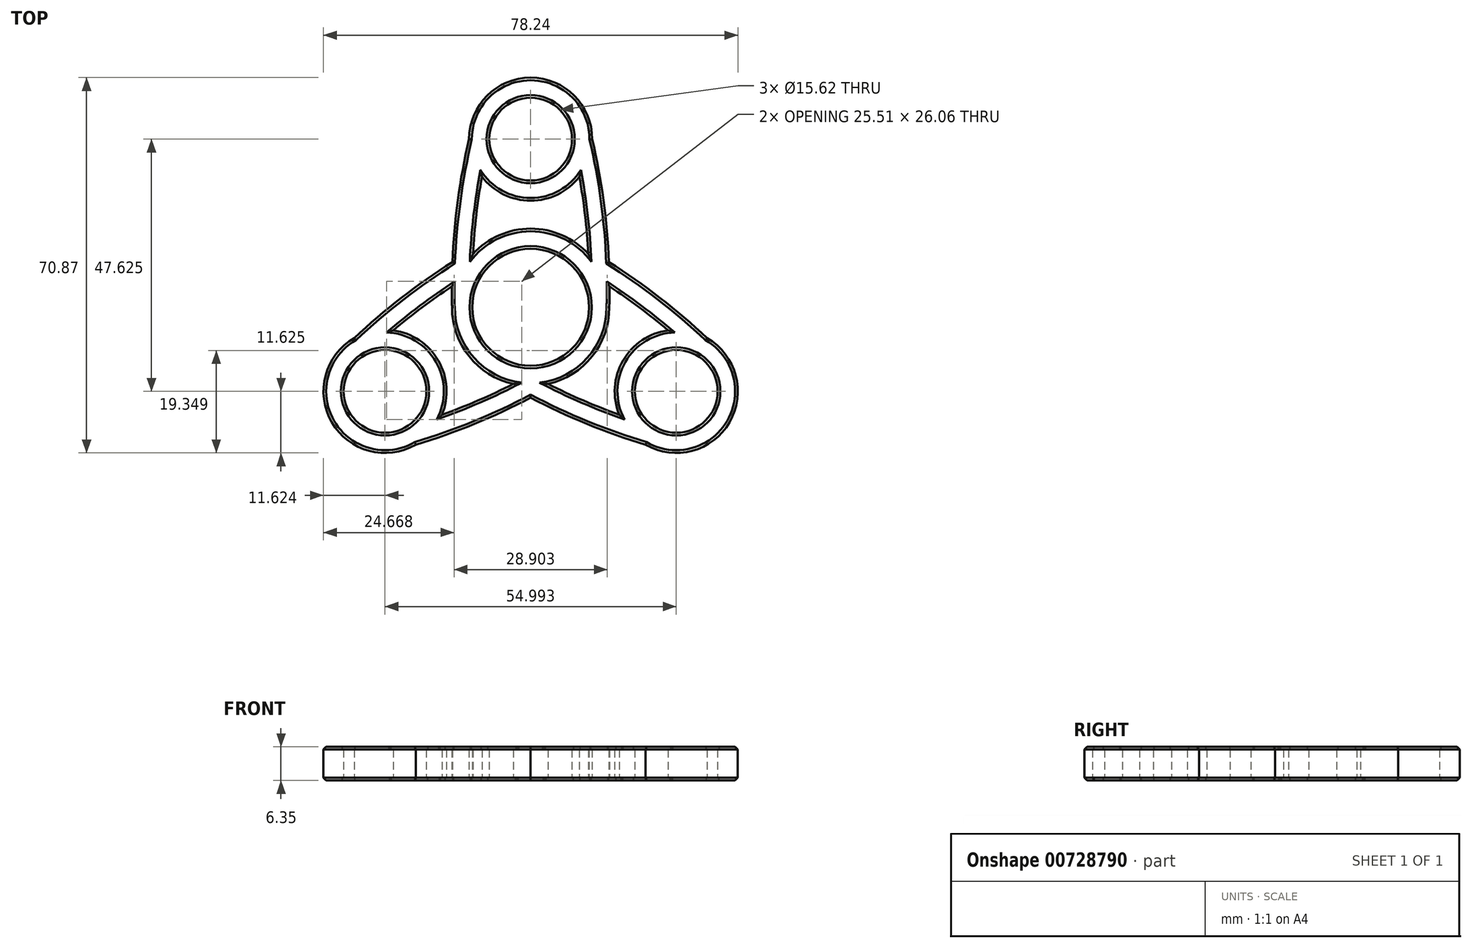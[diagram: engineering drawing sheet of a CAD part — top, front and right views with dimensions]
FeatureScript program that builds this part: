
annotation { "Feature Type Name" : "Feature", "Feature Type Description" : "" }
export const myFeature = defineFeature(function(context is Context, id is Id, definition is map)
    precondition{}
    {
        {
            var Q0;
            Q0=qCreatedBy(makeId("Top.planeOp"),FACE);
            var sketch = newSketch(context, id + "F0", { "sketchPlane" : qUnion([Q0])});
            skCircle(sketch, "E0", {"center": v(0, 0) * mm, "radius": 11.04 * mm});
            skPoint(sketch, "E1.orphan", {"position": v(-10.8, 40.16) * mm});
            skPoint(sketch, "E2.orphan", {"position": v(-5.54, 30.57) * mm});
            skPoint(sketch, "E3.orphan", {"position": v(10.8, 40.16) * mm});
            skPoint(sketch, "E4.start.orphan", {"position": v(0, 56) * mm});
            skCircle(sketch, "E5", {"center": v(0, 31.75) * mm, "radius": 7.81 * mm});
            skArc(sketch, "E6.0", {"start": v(-9.2, 24.65) * mm, "mid": v(0, 20.13) * mm, "end": v(9.2, 24.65) * mm});
            skArc(sketch, "E7.0", {"start": v(-14.85, 0) * mm, "mid": v(-11.6, -9.27) * mm, "end": v(-3.28, -14.48) * mm});
            skLineSegment(sketch, "E8", {"start": v(3.28, 31.75) * mm, "end": v(3.28, 31.75) * mm});
            skArc(sketch, "E9", {"start": v(-11.62, 31.75) * mm, "mid": v(-13.75, 20.22) * mm, "end": v(-14.79, 8.54) * mm});
            skArc(sketch, "E10.0", {"start": v(-9.2, 24.65) * mm, "mid": v(-10.27, 17.4) * mm, "end": v(-10.9, 10.08) * mm});
            skArc(sketch, "E11.MirrorCS", {"start": v(9.2, 24.65) * mm, "mid": v(10.27, 17.4) * mm, "end": v(10.9, 10.08) * mm});
            skArc(sketch, "E12.MirrorCS", {"start": v(11.62, 31.75) * mm, "mid": v(13.75, 20.22) * mm, "end": v(14.79, 8.54) * mm});
            skPoint(sketch, "E13.orphan", {"position": v(-7.91, 30.88) * mm});
            skPoint(sketch, "E14.orphan", {"position": v(-11.04, 0.1) * mm});
            skPoint(sketch, "E15.orphan", {"position": v(7.91, 30.88) * mm});
            skArc(sketch, "E16.trimOffspring", {"start": v(11.62, 31.75) * mm, "mid": v(0, 43.37) * mm, "end": v(-11.62, 31.75) * mm});
            skPoint(sketch, "E17.orphan", {"position": v(11.04, 0.1) * mm});
            skArc(sketch, "E18.trimOffspring", {"start": v(10.9, 10.08) * mm, "mid": v(0, 14.85) * mm, "end": v(-10.9, 10.08) * mm});
            skArc(sketch, "E19.1.0", {"start": v(-33.3, -5.81) * mm, "mid": v(-24.39, 1.8) * mm, "end": v(-14.79, 8.54) * mm});
            skArc(sketch, "E19.1.1", {"start": v(-25.95, -4.36) * mm, "mid": v(-20.54, -0.05) * mm, "end": v(-14.9, 3.93) * mm});
            skArc(sketch, "E19.1.2", {"start": v(-16.75, -20.3) * mm, "mid": v(-9.92, -17.6) * mm, "end": v(-3.28, -14.48) * mm});
            skArc(sketch, "E19.1.3", {"start": v(-16.75, -20.3) * mm, "mid": v(-17.43, -10.06) * mm, "end": v(-25.95, -4.36) * mm});
            skCircle(sketch, "E19.1.4", {"center": v(-27.5, -15.87) * mm, "radius": 7.81 * mm});
            skArc(sketch, "E19.1.5", {"start": v(-33.3, -5.81) * mm, "mid": v(-37.56, -21.69) * mm, "end": v(-21.69, -25.94) * mm});
            skArc(sketch, "E19.1.6", {"start": v(-21.69, -25.94) * mm, "mid": v(-10.63, -22.02) * mm, "end": v(0, -17.08) * mm});
            skArc(sketch, "E19.2.0", {"start": v(21.69, -25.94) * mm, "mid": v(10.63, -22.02) * mm, "end": v(0, -17.08) * mm});
            skArc(sketch, "E19.2.1", {"start": v(16.75, -20.3) * mm, "mid": v(9.92, -17.6) * mm, "end": v(3.28, -14.48) * mm});
            skArc(sketch, "E19.2.2", {"start": v(25.95, -4.36) * mm, "mid": v(20.54, -0.05) * mm, "end": v(14.9, 3.93) * mm});
            skArc(sketch, "E19.2.3", {"start": v(25.95, -4.36) * mm, "mid": v(17.43, -10.06) * mm, "end": v(16.75, -20.3) * mm});
            skCircle(sketch, "E19.2.4", {"center": v(27.5, -15.88) * mm, "radius": 7.81 * mm});
            skArc(sketch, "E19.2.5", {"start": v(21.69, -25.94) * mm, "mid": v(37.56, -21.69) * mm, "end": v(33.3, -5.81) * mm});
            skArc(sketch, "E19.2.6", {"start": v(33.3, -5.81) * mm, "mid": v(24.39, 1.8) * mm, "end": v(14.79, 8.54) * mm});
            skArc(sketch, "E20.trimOffspring", {"start": v(-14.9, 3.93) * mm, "mid": v(-14.89, 1.97) * mm, "end": v(-14.85, 0) * mm});
            skPoint(sketch, "E21.orphan", {"position": v(-14.18, 4.4) * mm});
            skPoint(sketch, "E22.orphan", {"position": v(7.42, -12.86) * mm});
            skArc(sketch, "E23.trimOffspring", {"start": v(3.28, -14.48) * mm, "mid": v(11.6, -9.27) * mm, "end": v(14.85, 0) * mm});
            skPoint(sketch, "E24.orphan", {"position": v(7.42, 12.86) * mm});
            skPoint(sketch, "E25.orphan", {"position": v(14.18, 4.4) * mm});
            skArc(sketch, "E26.trimOffspring", {"start": v(14.9, 3.93) * mm, "mid": v(14.89, 1.97) * mm, "end": v(14.85, 0) * mm});
            skSolve(sketch);
        }
        {
            var Q0;
            Q0=makeQuery(id+"F0.imprint","IMPRINT",FACE,{"disambiguationData":[TD([[makeQuery(id+"F0.imprint","IMPRINT",EDGE,{"derivedFrom":sQuery(id+"F0.wireOp",EDGE,"E0")}),-1.0]])]});
            extrude(context, id + "F1", {"entities" : qUnion([Q0]), "depth" : 6.35 * mm, "offsetDistance" : 25.4 * mm});
        }
        {
            var Q0;
            Q0=makeQuery(id+"F1.opExtrude","CAP_FACE",FACE,{"disambiguationData":[OSD([sQuery(id+"F0.wireOp",EDGE,"E0"),sQuery(id+"F0.wireOp",EDGE,"E5"),sQuery(id+"F0.wireOp",EDGE,"E6.0"),sQuery(id+"F0.wireOp",EDGE,"E7.0"),sQuery(id+"F0.wireOp",EDGE,"E9"),sQuery(id+"F0.wireOp",EDGE,"E10.0"),sQuery(id+"F0.wireOp",EDGE,"E11.MirrorCS"),sQuery(id+"F0.wireOp",EDGE,"E12.MirrorCS"),sQuery(id+"F0.wireOp",EDGE,"E16.trimOffspring"),sQuery(id+"F0.wireOp",EDGE,"E18.trimOffspring"),sQuery(id+"F0.wireOp",EDGE,"E19.1.0"),sQuery(id+"F0.wireOp",EDGE,"E19.1.1"),sQuery(id+"F0.wireOp",EDGE,"E19.1.2"),sQuery(id+"F0.wireOp",EDGE,"E19.1.3"),sQuery(id+"F0.wireOp",EDGE,"E19.1.4"),sQuery(id+"F0.wireOp",EDGE,"E19.1.5"),sQuery(id+"F0.wireOp",EDGE,"E19.1.6"),sQuery(id+"F0.wireOp",EDGE,"E19.2.0"),sQuery(id+"F0.wireOp",EDGE,"E19.2.1"),sQuery(id+"F0.wireOp",EDGE,"E19.2.2"),sQuery(id+"F0.wireOp",EDGE,"E19.2.3"),sQuery(id+"F0.wireOp",EDGE,"E19.2.4"),sQuery(id+"F0.wireOp",EDGE,"E19.2.5"),sQuery(id+"F0.wireOp",EDGE,"E19.2.6"),sQuery(id+"F0.wireOp",EDGE,"E20.trimOffspring"),sQuery(id+"F0.wireOp",EDGE,"E23.trimOffspring"),sQuery(id+"F0.wireOp",EDGE,"E26.trimOffspring")])],"isStart":false});
            var Q1;
            Q1=makeQuery(id+"F1.opExtrude","CAP_FACE",FACE,{"disambiguationData":[OSD([sQuery(id+"F0.wireOp",EDGE,"E0"),sQuery(id+"F0.wireOp",EDGE,"E5"),sQuery(id+"F0.wireOp",EDGE,"E6.0"),sQuery(id+"F0.wireOp",EDGE,"E7.0"),sQuery(id+"F0.wireOp",EDGE,"E9"),sQuery(id+"F0.wireOp",EDGE,"E10.0"),sQuery(id+"F0.wireOp",EDGE,"E11.MirrorCS"),sQuery(id+"F0.wireOp",EDGE,"E12.MirrorCS"),sQuery(id+"F0.wireOp",EDGE,"E16.trimOffspring"),sQuery(id+"F0.wireOp",EDGE,"E18.trimOffspring"),sQuery(id+"F0.wireOp",EDGE,"E19.1.0"),sQuery(id+"F0.wireOp",EDGE,"E19.1.1"),sQuery(id+"F0.wireOp",EDGE,"E19.1.2"),sQuery(id+"F0.wireOp",EDGE,"E19.1.3"),sQuery(id+"F0.wireOp",EDGE,"E19.1.4"),sQuery(id+"F0.wireOp",EDGE,"E19.1.5"),sQuery(id+"F0.wireOp",EDGE,"E19.1.6"),sQuery(id+"F0.wireOp",EDGE,"E19.2.0"),sQuery(id+"F0.wireOp",EDGE,"E19.2.1"),sQuery(id+"F0.wireOp",EDGE,"E19.2.2"),sQuery(id+"F0.wireOp",EDGE,"E19.2.3"),sQuery(id+"F0.wireOp",EDGE,"E19.2.4"),sQuery(id+"F0.wireOp",EDGE,"E19.2.5"),sQuery(id+"F0.wireOp",EDGE,"E19.2.6"),sQuery(id+"F0.wireOp",EDGE,"E20.trimOffspring"),sQuery(id+"F0.wireOp",EDGE,"E23.trimOffspring"),sQuery(id+"F0.wireOp",EDGE,"E26.trimOffspring")])],"isStart":true});
            chamfer(context, id + "F2", {"entities" : qUnion([Q0, Q1]), "width" : 0.5 * mm, "tangentPropagation" : true});
        }
    });
